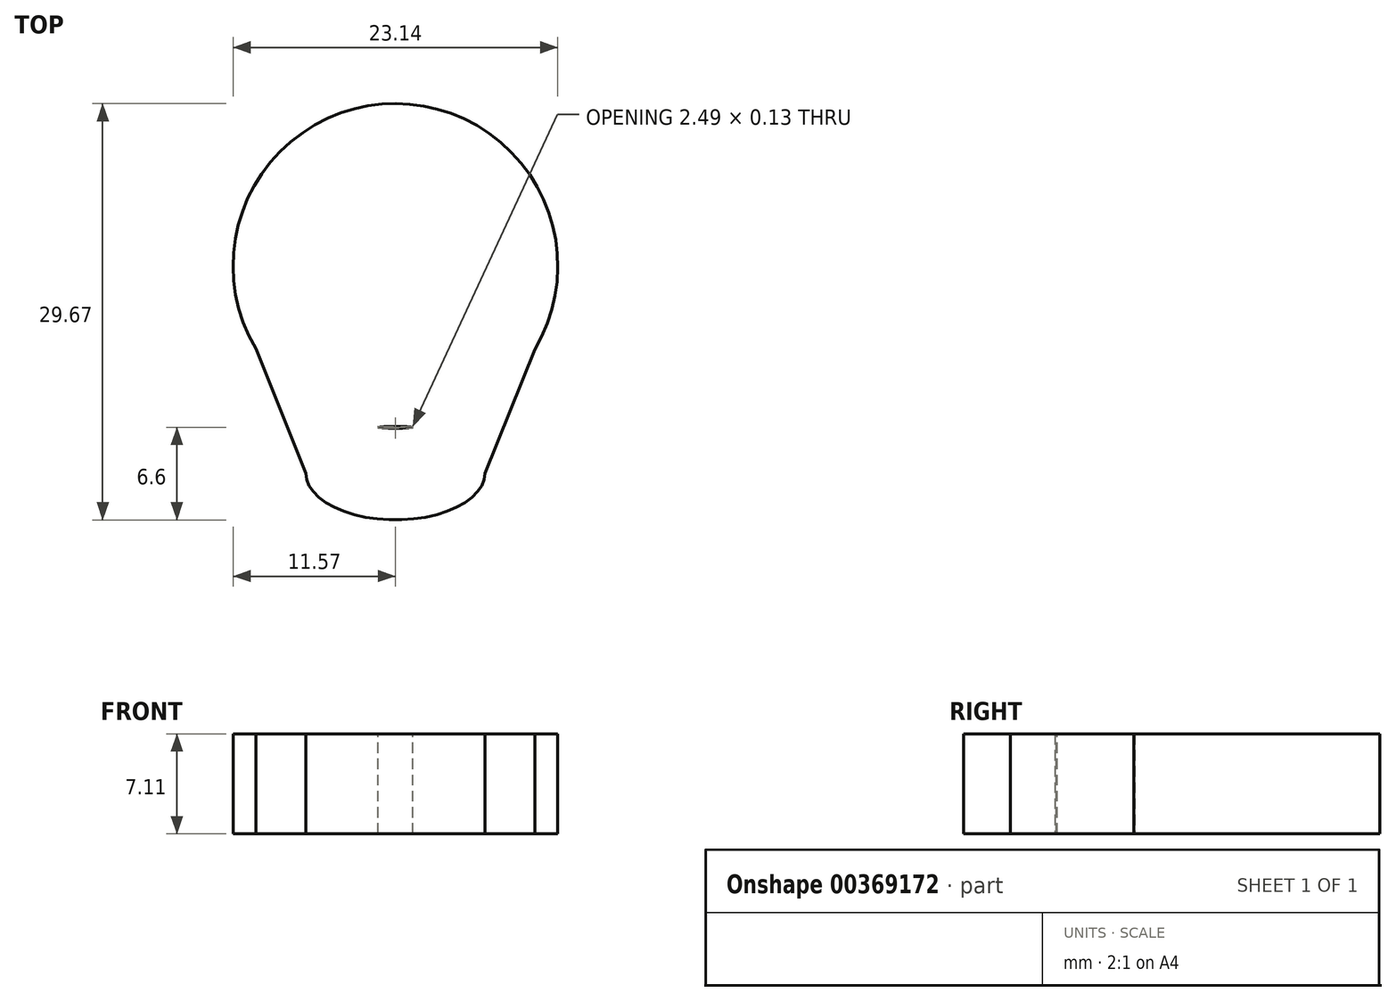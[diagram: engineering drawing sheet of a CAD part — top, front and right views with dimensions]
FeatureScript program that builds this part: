
annotation { "Feature Type Name" : "Feature", "Feature Type Description" : "" }
export const myFeature = defineFeature(function(context is Context, id is Id, definition is map)
    precondition{}
    {
        {
            var Q0;
            Q0=qCreatedBy(makeId("Top.planeOp"),FACE);
            var sketch = newSketch(context, id + "F0", { "sketchPlane" : qUnion([Q0])});
            skCircle(sketch, "E0", {"center": v(0, 46.98) * mm, "radius": 11.57 * mm});
            skLineSegment(sketch, "E1", {"start": v(0, 46.98) * mm, "end": v(0, 32.21) * mm});
            skEllipse(sketch, "E2", {"center": v(0, 32.21) * mm, "majorRadius": 6.38 * mm, "minorRadius": 3.33 * mm, "majorAxis": v(1, 0)});
            skLineSegment(sketch, "E3", {"start": v(-9.95, 41.09) * mm, "end": v(-6.38, 32.21) * mm});
            skLineSegment(sketch, "E4", {"start": v(-6.38, 32.21) * mm, "end": v(6.38, 32.21) * mm});
            skLineSegment(sketch, "E5", {"start": v(6.38, 32.21) * mm, "end": v(9.92, 41.03) * mm});
            skSolve(sketch);
        }
        {
            var Q0;
            {var subQ0=sQuery(id+"F0.wireOp",EDGE,"E0");var subQ1=makeQuery(id+"F0.imprint","INTERSECT",VERTEX,{"derivedFrom":[subQ0,sQuery(id+"F0.wireOp",EDGE,"E3")]});Q0=makeQuery(id+"F0.imprint","IMPRINT",FACE,{"disambiguationData":[TD([[makeQuery(id+"F0.imprint","IMPRINT",EDGE,{"disambiguationData":[TD([[subQ1,-1.0]])],"derivedFrom":subQ0}),1.0]])]});}
            var Q1;
            {var subQ0=sQuery(id+"F0.wireOp",EDGE,"E5");Q1=makeQuery(id+"F0.imprint","IMPRINT",FACE,{"disambiguationData":[TD([[makeQuery(id+"F0.imprint","IMPRINT",EDGE,{"derivedFrom":subQ0}),1.0]])]});}
            var Q2;
            {var subQ0=sQuery(id+"F0.wireOp",EDGE,"E2");var subQ1=sQuery(id+"F0.wireOp",EDGE,"E0");var subQ2=makeQuery(id+"F0.imprint","INTERSECT",VERTEX,{"disambiguationData":[OD(0.0)],"derivedFrom":[subQ1,subQ0]});Q2=makeQuery(id+"F0.imprint","IMPRINT",FACE,{"disambiguationData":[TD([[makeQuery(id+"F0.imprint","IMPRINT",EDGE,{"disambiguationData":[TD([[subQ2,-1.0]])],"derivedFrom":subQ1}),-1.0]])]});}
            var Q3;
            {var subQ0=sQuery(id+"F0.wireOp",EDGE,"E1");var subQ1=sQuery(id+"F0.wireOp",EDGE,"E0");var subQ2=makeQuery(id+"F0.imprint","INTERSECT",VERTEX,{"derivedFrom":[subQ1,subQ0]});Q3=makeQuery(id+"F0.imprint","IMPRINT",FACE,{"disambiguationData":[TD([[makeQuery(id+"F0.imprint","IMPRINT",EDGE,{"disambiguationData":[TD([[subQ2,-1.0]])],"derivedFrom":subQ1}),-1.0]])]});}
            var Q4;
            {var subQ0=sQuery(id+"F0.wireOp",EDGE,"E4");var subQ4=makeQuery(id+"F0.imprint","INTERSECT",VERTEX,{"derivedFrom":[sQuery(id+"F0.wireOp",EDGE,"E1"),subQ0]});Q4=makeQuery(id+"F0.imprint","IMPRINT",FACE,{"disambiguationData":[TD([[makeQuery(id+"F0.imprint","IMPRINT",EDGE,{"disambiguationData":[TD([[subQ4,1.0]])],"derivedFrom":subQ0}),-1.0]])]});}
            var Q5;
            {var subQ0=sQuery(id+"F0.wireOp",EDGE,"E3");Q5=makeQuery(id+"F0.imprint","IMPRINT",FACE,{"disambiguationData":[TD([[makeQuery(id+"F0.imprint","IMPRINT",EDGE,{"derivedFrom":subQ0}),1.0]])]});}
            extrude(context, id + "F1", {"entities" : qUnion([Q0, Q1, Q2, Q3, Q4, Q5]), "depth" : 7.11 * mm});
        }
    });
